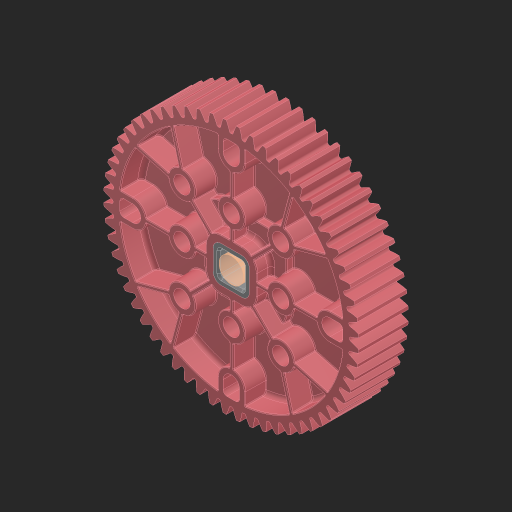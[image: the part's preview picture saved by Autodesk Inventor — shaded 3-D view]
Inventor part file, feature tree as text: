
AUTODESK INVENTOR PART (.ipt)
format: ipt  version: 2023 (Build 270158000, 158)  size: 3,452,928 bytes
history: native  units: in
note: dims shown in document units (in); Inventor stores cm internally (conversion verified against a paired STEP export)
features: other x3, sketch x1, extrude x1
ambient origin geometry x8: Origin, YZ Plane, XZ Plane, XY Plane, X Axis, Y Axis, Z Axis, Center Point
bodies: Solid1 (feature_tree), Solid2 (feature_tree)
feature tree (5):
  sketch  "Sketch1"  dims[d0=0.25in d1=0.3937in d2=0.0in d3=0.0197in d4=0.0344in]
  other  "Srf1"
  other  "276-7748-001_OVERMOLD Rev3_60T 24DP Gear Rev1_1:1"
  other  "276-7573-002 Rev7_2:1"
  extrude  "ExtrusionSrf1"  Depth=0.3937in TaperAngle=0.0deg
